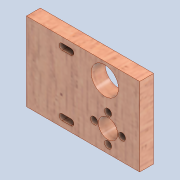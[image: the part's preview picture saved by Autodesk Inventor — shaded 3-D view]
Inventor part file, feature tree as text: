
AUTODESK INVENTOR PART (.ipt)
format: ipt  version: 2020 (Build 240168000, 168)  size: 243,712 bytes
history: native  units: mm
features: extrude x4, sketch x4, other x2, projected_geometry x1, reference x1
ambient origin geometry x8: Origin, YZ Plane, XZ Plane, XY Plane, X Axis, Y Axis, Z Axis, Center Point
bodies: Solid1 (feature_tree)
feature tree (12):
  extrude  "Extrusion1"  Depth=45.0mm
  extrude  "Extrusion3"  Depth=8.0mm
  extrude  "Extrusion4"  Depth=3.5mm
  extrude  "Extrusion5"  TaperAngle=0.0deg  [1 undecoded]
  sketch  "Sketch1"  dims[d0=65.0mm d1=45.0mm]
  sketch  "Sketch3"  dims[d2=8.0mm d3=0.0mm d8=5.0mm]
  projected_geometry  "Projected Loop1"
  sketch  "Sketch4"  dims[d9=3.5mm d10=5.0mm]
  sketch  "Sketch5"  dims[d12=0.0mm d13=0.0mm d14=0.0mm d15=0.0mm d16=5.0mm d17=23.0mm d18=5.0mm d19=8.0mm d20=11.0mm d21=4.1mm d22=4.1mm d23=4.1mm d24=4.1mm d25=22.0mm d26=18.139532mm d27=8.0mm d28=8.0mm d29=8.0mm d30=12.5mm d31=15.7mm d32=23.0mm d33=20.0mm d34=10.0mm d35=0.0mm d36=23.0mm]
  reference  "Reference4"
  other  "0005-10-04 Z axis and extruder.iam"
  other  "0005-10-004 Actionare 2 seringa.ipt:42"
note: 1 required parameter value undecoded (feature->parameter linkage not recoverable at this tier; creation-order binding heuristic only, values carry confidence <= 0.55)
